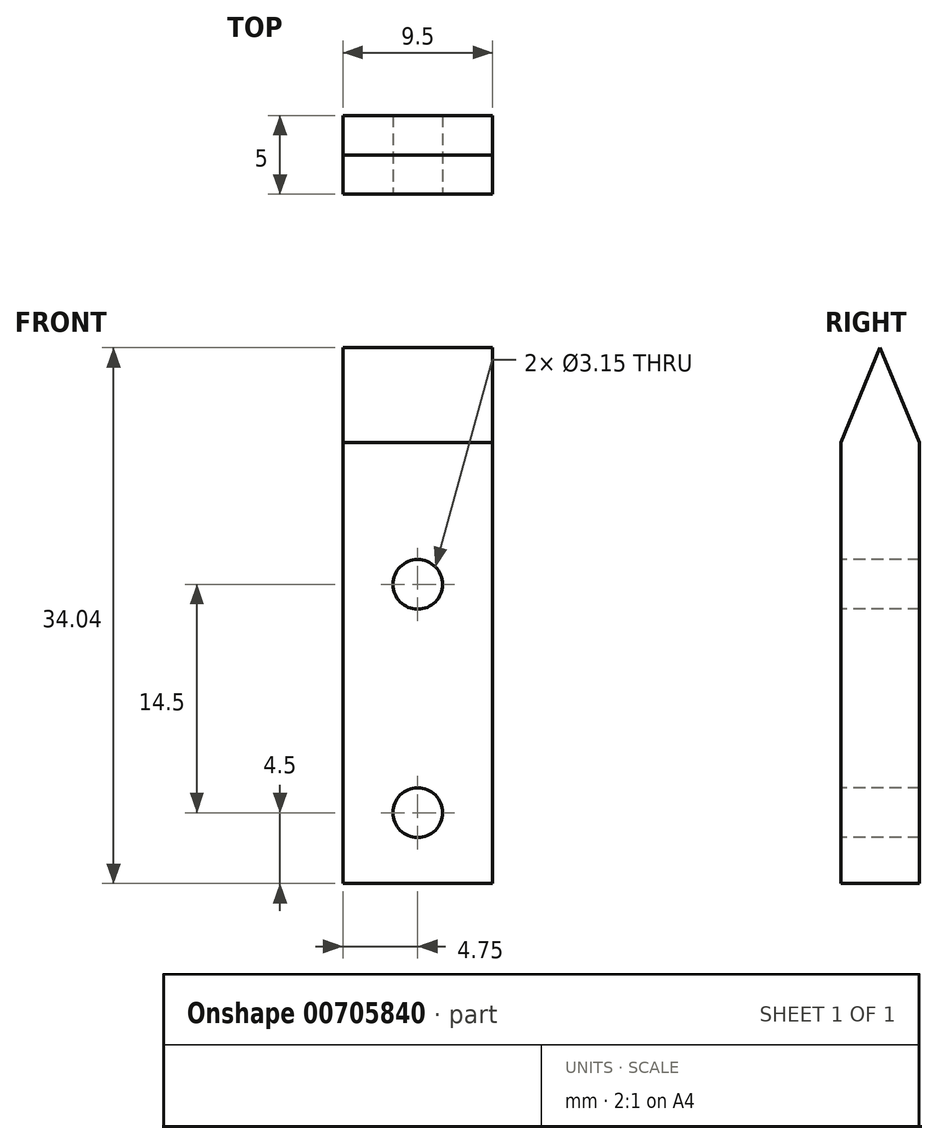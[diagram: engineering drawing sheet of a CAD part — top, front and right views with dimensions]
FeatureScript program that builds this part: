
annotation { "Feature Type Name" : "Feature", "Feature Type Description" : "" }
export const myFeature = defineFeature(function(context is Context, id is Id, definition is map)
    precondition{}
    {
        {
            var Q0;
            Q0=qCreatedBy(makeId("Right.planeOp"),FACE);
            var sketch = newSketch(context, id + "F0", { "sketchPlane" : qUnion([Q0])});
            skLineSegment(sketch, "E0", {"start": v(0, 0) * mm, "end": v(0, 28) * mm});
            skLineSegment(sketch, "E1", {"start": v(0, 28) * mm, "end": v(2.48, 34.04) * mm});
            skLineSegment(sketch, "E2", {"start": v(2.48, 34.04) * mm, "end": v(5, 28) * mm});
            skLineSegment(sketch, "E3", {"start": v(5, 28) * mm, "end": v(5, 0) * mm});
            skLineSegment(sketch, "E4", {"start": v(5, 0) * mm, "end": v(0, 0) * mm});
            skSolve(sketch);
        }
        {
            var Q0;
            Q0 = qSketchRegion(id + "F0", true);
            extrude(context, id + "F1", {"entities" : qUnion([Q0]), "depth" : 9.5 * mm, "offsetDistance" : 25 * mm});
        }
        {
            var Q0;
            Q0=makeQuery(id+"F1.opExtrude","SWEPT_FACE",FACE,{"disambiguationData":[OSD([sQuery(id+"F0.wireOp",EDGE,"E0")])]});
            var sketch = newSketch(context, id + "F2", { "sketchPlane" : qUnion([Q0])});
            skPoint(sketch, "E5", {"position": v(4.75, 4.5) * mm});
            skPoint(sketch, "E6", {"position": v(4.75, 19) * mm});
            skSolve(sketch);
        }
        {
            var Q0;
            Q0=sQuery(id+"F2.wireOp",VERTEX,"E6");
            var Q1;
            Q1=sQuery(id+"F2.wireOp",VERTEX,"E5");
            var Q2;
            Q2=makeQuery(id+"F1.opExtrude","SWEPT_BODY",BODY,{"disambiguationData":[OSD([sQuery(id+"F0.wireOp",EDGE,"E0"),sQuery(id+"F0.wireOp",EDGE,"E1"),sQuery(id+"F0.wireOp",EDGE,"E2"),sQuery(id+"F0.wireOp",EDGE,"E3"),sQuery(id+"F0.wireOp",EDGE,"E4")])]});
            hole(context, id + "F3", {"style" : HoleStyle.SIMPLE, "endStyle" : HoleEndStyle.THROUGH, "standardTappedOrClearance" : lookupTablePath({ "standard" : "ISO", "fit" : "Close", "size" : "M3", "type" : "Clearance" }), "standardBlindInLast" : lookupTablePath({ "fit" : "Close", "standard" : "ISO", "size" : "M3", "type" : "Clearance" }), "holeDiameter" : 3.15 * mm, "majorDiameter" : 10 * mm, "isTappedThrough" : true, "tappedDepth" : 21.25 * mm, "tapClearance" : 3, "startFromSketch" : true, "locations" : qUnion([Q0, Q1]), "scope" : qUnion([Q2])});
        }
    });
